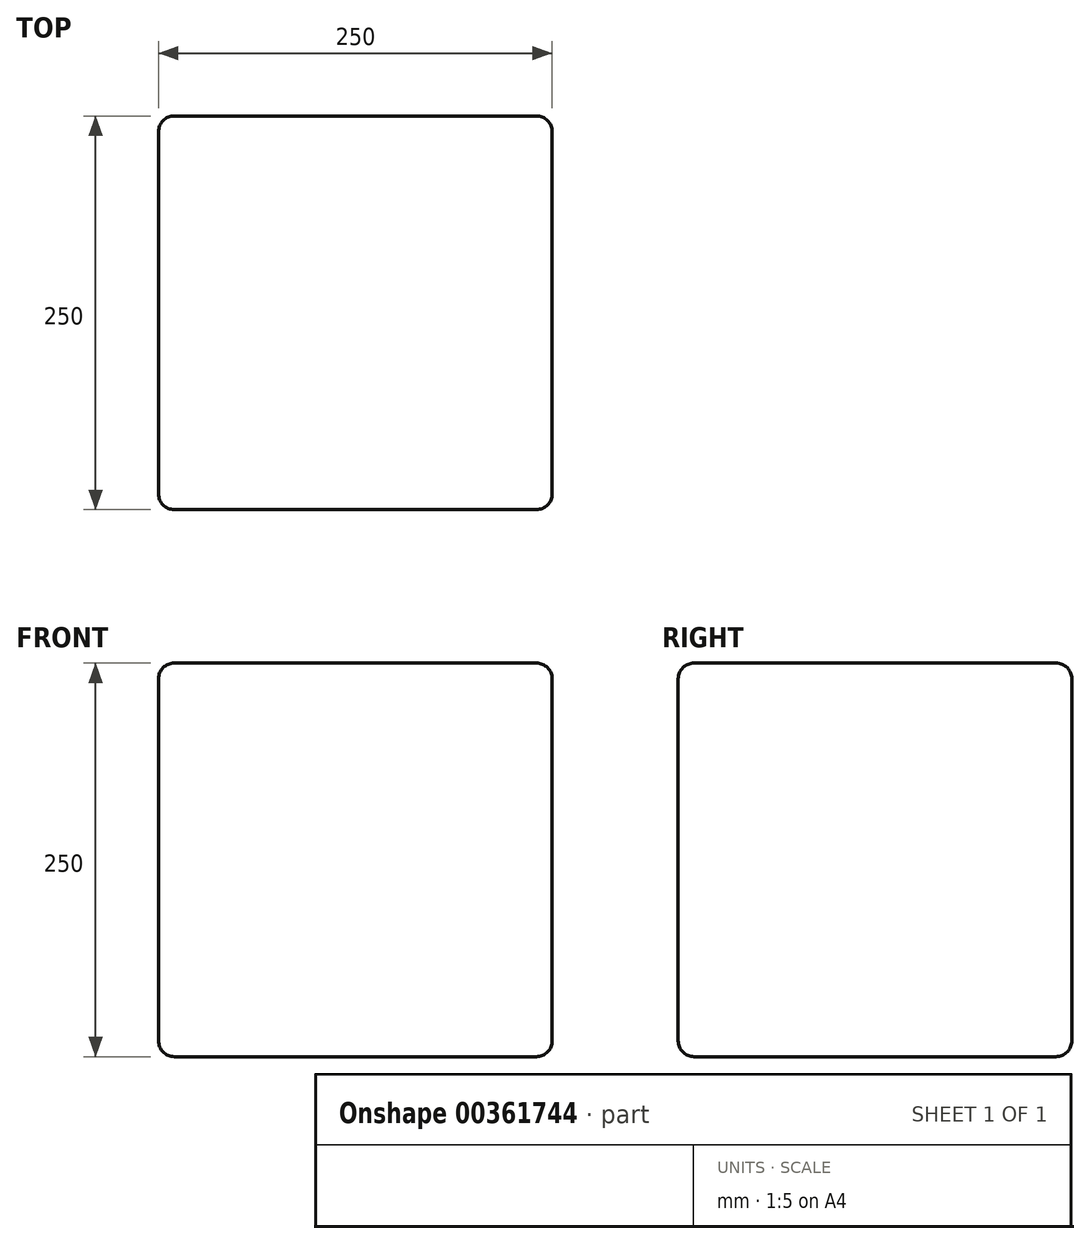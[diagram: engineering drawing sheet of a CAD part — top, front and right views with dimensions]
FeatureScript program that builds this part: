
annotation { "Feature Type Name" : "Feature", "Feature Type Description" : "" }
export const myFeature = defineFeature(function(context is Context, id is Id, definition is map)
    precondition{}
    {
        {
            var Q0;
            Q0=qCreatedBy(makeId("Top.planeOp"),FACE);
            var sketch = newSketch(context, id + "F0", { "sketchPlane" : qUnion([Q0])});
            skLineSegment(sketch, "E0.bottom", {"start": v(-124.1, -108.78) * mm, "end": v(125.9, -108.78) * mm});
            skLineSegment(sketch, "E0.top", {"start": v(-124.1, 141.22) * mm, "end": v(125.9, 141.22) * mm});
            skLineSegment(sketch, "E0.left", {"start": v(-124.1, -108.78) * mm, "end": v(-124.1, 141.22) * mm});
            skLineSegment(sketch, "E0.right", {"start": v(125.9, -108.78) * mm, "end": v(125.9, 141.22) * mm});
            skSolve(sketch);
        }
        {
            var Q0;
            Q0=makeQuery(id+"F0.imprint","IMPRINT",FACE,{"disambiguationData":[TD([[makeQuery(id+"F0.imprint","IMPRINT",EDGE,{"derivedFrom":sQuery(id+"F0.wireOp",EDGE,"E0.bottom")}),1.0]])]});
            extrude(context, id + "F1", {"entities" : qUnion([Q0]), "depth" : 250 * mm});
        }
        {
            var Q0;
            Q0=makeQuery(id+"F1.opExtrude","SWEPT_EDGE",EDGE,{"disambiguationData":[OSD([sQuery(id+"F0.wireOp",EDGE,"E0.top"),sQuery(id+"F0.wireOp",EDGE,"E0.left")])]});
            var Q1;
            Q1=makeQuery(id+"F1.opExtrude","CAP_FACE",FACE,{"disambiguationData":[OSD([sQuery(id+"F0.wireOp",EDGE,"E0.bottom"),sQuery(id+"F0.wireOp",EDGE,"E0.top"),sQuery(id+"F0.wireOp",EDGE,"E0.left"),sQuery(id+"F0.wireOp",EDGE,"E0.right")])],"isStart":false});
            var Q2;
            Q2=makeQuery(id+"F1.opExtrude","SWEPT_FACE",FACE,{"disambiguationData":[OSD([sQuery(id+"F0.wireOp",EDGE,"E0.left")])]});
            var Q3;
            Q3=makeQuery(id+"F1.opExtrude","SWEPT_FACE",FACE,{"disambiguationData":[OSD([sQuery(id+"F0.wireOp",EDGE,"E0.bottom")])]});
            var Q4;
            Q4=makeQuery(id+"F1.opExtrude","SWEPT_FACE",FACE,{"disambiguationData":[OSD([sQuery(id+"F0.wireOp",EDGE,"E0.right")])]});
            var Q5;
            Q5=makeQuery(id+"F1.opExtrude","CAP_EDGE",EDGE,{"disambiguationData":[OSD([sQuery(id+"F0.wireOp",EDGE,"E0.top")])],"isStart":true});
            fillet(context, id + "F2", {"entities" : qUnion([Q0, Q1, Q2, Q3, Q4, Q5]), "radius" : 10 * mm, "tangentPropagation" : true, "allowEdgeOverflow" : false});
        }
    });
